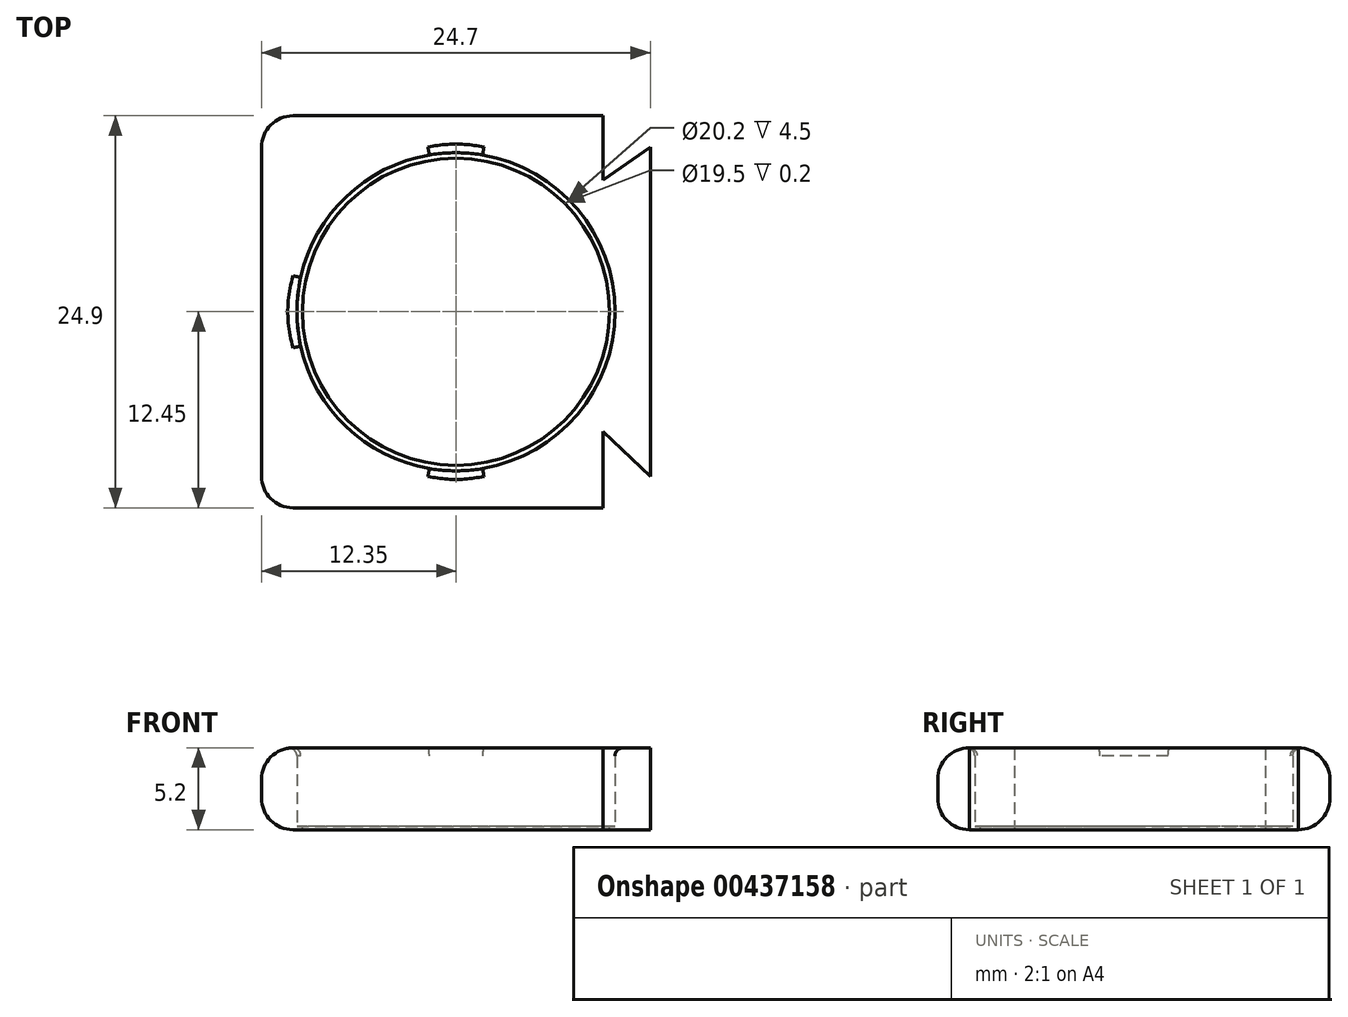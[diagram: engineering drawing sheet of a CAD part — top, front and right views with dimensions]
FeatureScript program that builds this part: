
annotation { "Feature Type Name" : "Feature", "Feature Type Description" : "" }
export const myFeature = defineFeature(function(context is Context, id is Id, definition is map)
    precondition{}
    {
        {
            var Q0;
            Q0=qCreatedBy(makeId("Top.planeOp"),FACE);
            var sketch = newSketch(context, id + "F0", { "sketchPlane" : qUnion([Q0])});
            skLineSegment(sketch, "E0.bottom", {"start": v(12.35, -12.45) * mm, "end": v(-12.35, -12.45) * mm});
            skLineSegment(sketch, "E0.top", {"start": v(12.35, 12.45) * mm, "end": v(-12.35, 12.45) * mm});
            skLineSegment(sketch, "E0.left", {"start": v(12.35, -12.45) * mm, "end": v(12.35, 12.45) * mm});
            skLineSegment(sketch, "E0.right", {"start": v(-12.35, -12.45) * mm, "end": v(-12.35, 12.45) * mm});
            skPoint(sketch, "E0.middle", {"position": v(0, 0) * mm});
            skCircle(sketch, "E1", {"center": v(0, 0) * mm, "radius": 9.75 * mm});
            skCircle(sketch, "E2", {"center": v(0, 0) * mm, "radius": 10.1 * mm});
            skLineSegment(sketch, "E3", {"start": v(9.35, -7.6) * mm, "end": v(9.35, -12.45) * mm});
            skLineSegment(sketch, "E4", {"start": v(9.35, 8.35) * mm, "end": v(9.35, 12.45) * mm});
            skLineSegment(sketch, "E5", {"start": v(9.35, 8.35) * mm, "end": v(12.35, 10.45) * mm});
            skLineSegment(sketch, "E6", {"start": v(9.35, -7.6) * mm, "end": v(12.35, -10.45) * mm});
            skSolve(sketch);
        }
        {
            var Q0;
            {var subQ0=sQuery(id+"F0.wireOp",EDGE,"E0.right");Q0=makeQuery(id+"F0.imprint","IMPRINT",FACE,{"disambiguationData":[TD([[makeQuery(id+"F0.imprint","IMPRINT",EDGE,{"derivedFrom":subQ0}),-1.0]])]});}
            extrude(context, id + "F1", {"entities" : qUnion([Q0]), "offsetDistance" : 25 * mm, "depth" : 5 * mm});
        }
        {
            var Q0;
            {var subQ0=sQuery(id+"F0.wireOp",EDGE,"E0.right");Q0=makeQuery(id+"F0.imprint","IMPRINT",FACE,{"disambiguationData":[TD([[makeQuery(id+"F0.imprint","IMPRINT",EDGE,{"derivedFrom":subQ0}),-1.0]])]});}
            var Q1;
            Q1=makeQuery(id+"F0.imprint","IMPRINT",FACE,{"disambiguationData":[TD([[makeQuery(id+"F0.imprint","IMPRINT",EDGE,{"derivedFrom":sQuery(id+"F0.wireOp",EDGE,"E1")}),-1.0]])]});
            extrude(context, id + "F2", {"entities" : qUnion([Q0, Q1]), "operationType" : NewBodyOperationType.ADD, "oppositeDirection" : true, "offsetDistance" : 25 * mm, "depth" : 0.2 * mm});
        }
        {
            var Q0;
            Q0=makeQuery(id+"F1.opExtrude","CAP_EDGE",EDGE,{"disambiguationData":[OSD([sQuery(id+"F0.wireOp",EDGE,"E0.right")])],"isStart":false});
            var Q1;
            Q1=makeQuery(id+"F1.opExtrude","CAP_EDGE",EDGE,{"disambiguationData":[OSD([sQuery(id+"F0.wireOp",EDGE,"E0.top")])],"isStart":false});
            var Q2;
            Q2=makeQuery(id+"F1.opExtrude","CAP_EDGE",EDGE,{"disambiguationData":[OSD([sQuery(id+"F0.wireOp",EDGE,"E0.bottom")])],"isStart":false});
            var Q3;
            {var subQ0=sQuery(id+"F0.wireOp",EDGE,"E0.top");Q3=makeQuery(id+"F2.boolean.opBoolean","MERGE",EDGE,{"derivedFrom":[makeQuery(id+"F1.opExtrude","CAP_EDGE",EDGE,{"disambiguationData":[OSD([subQ0])],"isStart":true}),makeQuery(id+"F2.opExtrude","CAP_EDGE",EDGE,{"disambiguationData":[OSD([subQ0])],"isStart":true})]});}
            var Q4;
            Q4=makeQuery(id+"F1.opExtrude","CAP_EDGE",EDGE,{"disambiguationData":[OSD([sQuery(id+"F0.wireOp",EDGE,"E0.right")])],"isStart":true});
            var Q5;
            {var subQ0=sQuery(id+"F0.wireOp",EDGE,"E0.bottom");Q5=makeQuery(id+"F2.boolean.opBoolean","MERGE",EDGE,{"derivedFrom":[makeQuery(id+"F1.opExtrude","CAP_EDGE",EDGE,{"disambiguationData":[OSD([subQ0])],"isStart":true}),makeQuery(id+"F2.opExtrude","CAP_EDGE",EDGE,{"disambiguationData":[OSD([subQ0])],"isStart":true})]});}
            var Q6;
            Q6=makeQuery(id+"F2.opExtrude","CAP_EDGE",EDGE,{"disambiguationData":[OSD([sQuery(id+"F0.wireOp",EDGE,"E0.bottom")])],"isStart":false});
            var Q7;
            Q7=makeQuery(id+"F2.opExtrude","CAP_EDGE",EDGE,{"disambiguationData":[OSD([sQuery(id+"F0.wireOp",EDGE,"E0.right")])],"isStart":false});
            var Q8;
            Q8=makeQuery(id+"F2.opExtrude","CAP_EDGE",EDGE,{"disambiguationData":[OSD([sQuery(id+"F0.wireOp",EDGE,"E0.top")])],"isStart":false});
            var Q9;
            {var subQ0=sQuery(id+"F0.wireOp",EDGE,"E0.right");var subQ1=sQuery(id+"F0.wireOp",EDGE,"E0.top");Q9=makeQuery(id+"F2.boolean.opBoolean","MERGE",EDGE,{"derivedFrom":[makeQuery(id+"F1.opExtrude","SWEPT_EDGE",EDGE,{"disambiguationData":[OSD([subQ1,subQ0])]}),makeQuery(id+"F2.opExtrude","SWEPT_EDGE",EDGE,{"disambiguationData":[OSD([subQ1,subQ0])]})]});}
            var Q10;
            {var subQ0=sQuery(id+"F0.wireOp",EDGE,"E0.right");var subQ1=sQuery(id+"F0.wireOp",EDGE,"E0.bottom");Q10=makeQuery(id+"F2.boolean.opBoolean","MERGE",EDGE,{"derivedFrom":[makeQuery(id+"F1.opExtrude","SWEPT_EDGE",EDGE,{"disambiguationData":[OSD([subQ1,subQ0])]}),makeQuery(id+"F2.opExtrude","SWEPT_EDGE",EDGE,{"disambiguationData":[OSD([subQ1,subQ0])]})]});}
            fillet(context, id + "F3", {"entities" : qUnion([Q0, Q1, Q2, Q3, Q4, Q5, Q6, Q7, Q8, Q9, Q10]), "radius" : 2 * mm, "tangentPropagation" : true, "allowEdgeOverflow" : false});
        }
        {
            var Q0;
            Q0=makeQuery(id+"F1.opExtrude","CAP_EDGE",EDGE,{"disambiguationData":[OSD([sQuery(id+"F0.wireOp",EDGE,"E2")])],"isStart":false});
            fillet(context, id + "F4", {"entities" : qUnion([Q0]), "radius" : 0.5 * mm, "tangentPropagation" : true, "allowEdgeOverflow" : false});
        }
    });
